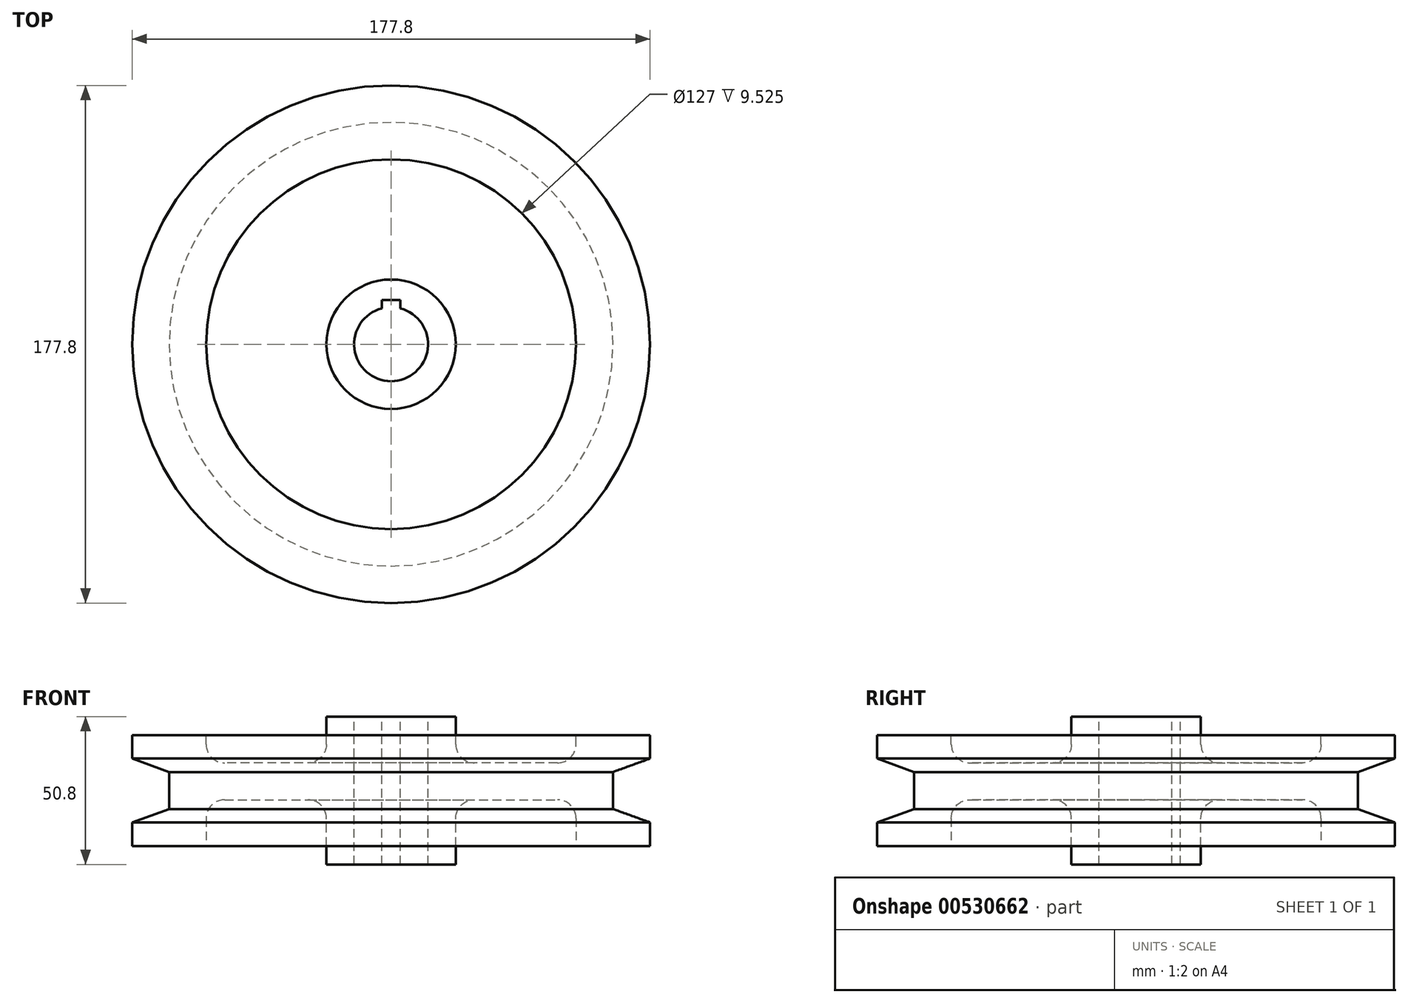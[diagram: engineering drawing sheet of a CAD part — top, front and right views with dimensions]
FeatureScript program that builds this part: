
annotation { "Feature Type Name" : "Feature", "Feature Type Description" : "" }
export const myFeature = defineFeature(function(context is Context, id is Id, definition is map)
    precondition{}
    {
        {
            var Q0;
            Q0=qCreatedBy(makeId("Front.planeOp"),FACE);
            var sketch = newSketch(context, id + "F0", { "sketchPlane" : qUnion([Q0])});
            skLineSegment(sketch, "E0.top", {"start": v(-69.65, -24.43) * mm, "end": v(-47.43, -24.43) * mm});
            skLineSegment(sketch, "E0.left", {"start": v(-69.65, 26.37) * mm, "end": v(-69.65, -24.43) * mm});
            skLineSegment(sketch, "E1.bottom", {"start": v(-47.43, 20.02) * mm, "end": v(19.25, 20.02) * mm});
            skLineSegment(sketch, "E1.top", {"start": v(-47.43, -18.08) * mm, "end": v(19.25, -18.08) * mm});
            skLineSegment(sketch, "E1.right", {"start": v(19.25, 20.02) * mm, "end": v(19.25, 11.94) * mm});
            skLineSegment(sketch, "E2", {"start": v(-47.43, -24.43) * mm, "end": v(-47.43, -18.08) * mm});
            skLineSegment(sketch, "E3", {"start": v(-69.65, 26.37) * mm, "end": v(-47.43, 26.37) * mm});
            skLineSegment(sketch, "E4", {"start": v(6.55, 7.32) * mm, "end": v(6.55, -5.38) * mm});
            skLineSegment(sketch, "E5", {"start": v(6.55, 7.32) * mm, "end": v(19.25, 11.94) * mm});
            skLineSegment(sketch, "E6", {"start": v(6.55, -5.38) * mm, "end": v(19.25, -10) * mm});
            skLineSegment(sketch, "E7", {"start": v(-69.65, 0.97) * mm, "end": v(28.04, 0.97) * mm, "construction": true});
            skPoint(sketch, "E7.endSnap0", {"position": v(-69.65, 0.97) * mm});
            skLineSegment(sketch, "E8.trimOffspring", {"start": v(19.25, -10) * mm, "end": v(19.25, -18.08) * mm});
            skLineSegment(sketch, "E9.trimOffspring", {"start": v(-47.43, 20.02) * mm, "end": v(-47.43, 26.37) * mm});
            skSolve(sketch);
        }
        {
            var Q0;
            Q0=makeQuery(id+"F0.imprint","IMPRINT",FACE,{"disambiguationData":[TD([[makeQuery(id+"F0.imprint","IMPRINT",EDGE,{"derivedFrom":sQuery(id+"F0.wireOp",EDGE,"E0.top")}),1.0]])]});
            var Q1;
            Q1=sQuery(id+"F0.wireOp",EDGE,"E0.left");
            revolve(context, id + "F1", {"entities" : qUnion([Q0]), "axis" : qUnion([Q1]), "revolveType" : RevolveType.FULL});
        }
        {
            var Q0;
            Q0=makeQuery(id+"F1.opRevolve","SWEPT_FACE",FACE,{"disambiguationData":[OSD([sQuery(id+"F0.wireOp",EDGE,"E3")])]});
            var sketch = newSketch(context, id + "F2", { "sketchPlane" : qUnion([Q0])});
            skArc(sketch, "E10", {"start": v(-72.83, 12.3) * mm, "mid": v(-69.65, -12.7) * mm, "end": v(-66.48, 12.3) * mm});
            skLineSegment(sketch, "E11", {"start": v(-69.65, -33.55) * mm, "end": v(-69.65, 36.25) * mm, "construction": true});
            skLineSegment(sketch, "E12.bottom", {"start": v(-72.83, 15.24) * mm, "end": v(-66.48, 15.24) * mm});
            skLineSegment(sketch, "E12.left", {"start": v(-72.83, 15.24) * mm, "end": v(-72.83, 12.3) * mm});
            skLineSegment(sketch, "E12.right", {"start": v(-66.48, 15.24) * mm, "end": v(-66.48, 12.3) * mm});
            skCircle(sketch, "E13", {"center": v(-69.65, 0) * mm, "radius": 63.5 * mm});
            skSolve(sketch);
        }
        {
            var Q0;
            Q0=makeQuery(id+"F2.imprint","IMPRINT",FACE,{"disambiguationData":[TD([[makeQuery(id+"F2.imprint","IMPRINT",EDGE,{"derivedFrom":sQuery(id+"F2.wireOp",EDGE,"E10")}),1.0]])]});
            extrude(context, id + "F3", {"entities" : qUnion([Q0]), "operationType" : NewBodyOperationType.REMOVE, "endBound" : BoundingType.THROUGH_ALL, "oppositeDirection" : true, "depth" : 25.4 * mm, "offsetDistance" : 25.4 * mm});
        }
        {
            var Q0;
            Q0=makeQuery(id+"F2.imprint","IMPRINT",FACE,{"disambiguationData":[TD([[makeQuery(id+"F2.imprint","IMPRINT",EDGE,{"derivedFrom":sQuery(id+"F2.wireOp",EDGE,"E13")}),1.0]])]});
            extrude(context, id + "F4", {"entities" : qUnion([Q0]), "operationType" : NewBodyOperationType.REMOVE, "oppositeDirection" : true, "depth" : 15.88 * mm, "offsetDistance" : 25.4 * mm});
        }
        {
            var Q0;
            Q0=makeQuery(id+"F1.opRevolve","SWEPT_FACE",FACE,{"disambiguationData":[OSD([sQuery(id+"F0.wireOp",EDGE,"E1.top")])]});
            var sketch = newSketch(context, id + "F5", { "sketchPlane" : qUnion([Q0])});
            skCircle(sketch, "E14", {"center": v(-69.65, 0) * mm, "radius": 63.5 * mm});
            skSolve(sketch);
        }
        {
            var Q0;
            Q0=makeQuery(id+"F5.imprint","IMPRINT",FACE,{"disambiguationData":[TD([[makeQuery(id+"F5.imprint","IMPRINT",EDGE,{"derivedFrom":sQuery(id+"F5.wireOp",EDGE,"E14")}),1.0]])]});
            extrude(context, id + "F6", {"entities" : qUnion([Q0]), "operationType" : NewBodyOperationType.REMOVE, "oppositeDirection" : true, "depth" : 15.88 * mm, "offsetDistance" : 25.4 * mm});
        }
        {
            var Q0;
            Q0=makeQuery(id+"F4.boolean.opBoolean","COPY",FACE,{"derivedFrom":makeQuery(id+"F4.opExtrude","CAP_FACE",FACE,{"disambiguationData":[OSD([sQuery(id+"F0.wireOp",EDGE,"E3"),sQuery(id+"F0.wireOp",EDGE,"E9.trimOffspring"),sQuery(id+"F2.wireOp",EDGE,"E13")])],"isStart":false})});
            var Q1;
            Q1=makeQuery(id+"F6.boolean.opBoolean","COPY",FACE,{"derivedFrom":makeQuery(id+"F6.opExtrude","CAP_FACE",FACE,{"disambiguationData":[OSD([sQuery(id+"F0.wireOp",EDGE,"E1.top"),sQuery(id+"F0.wireOp",EDGE,"E2"),sQuery(id+"F5.wireOp",EDGE,"E14")])],"isStart":false})});
            fillet(context, id + "F7", {"entities" : qUnion([Q0, Q1]), "radius" : 6.35 * mm, "tangentPropagation" : true, "allowEdgeOverflow" : false});
        }
    });
